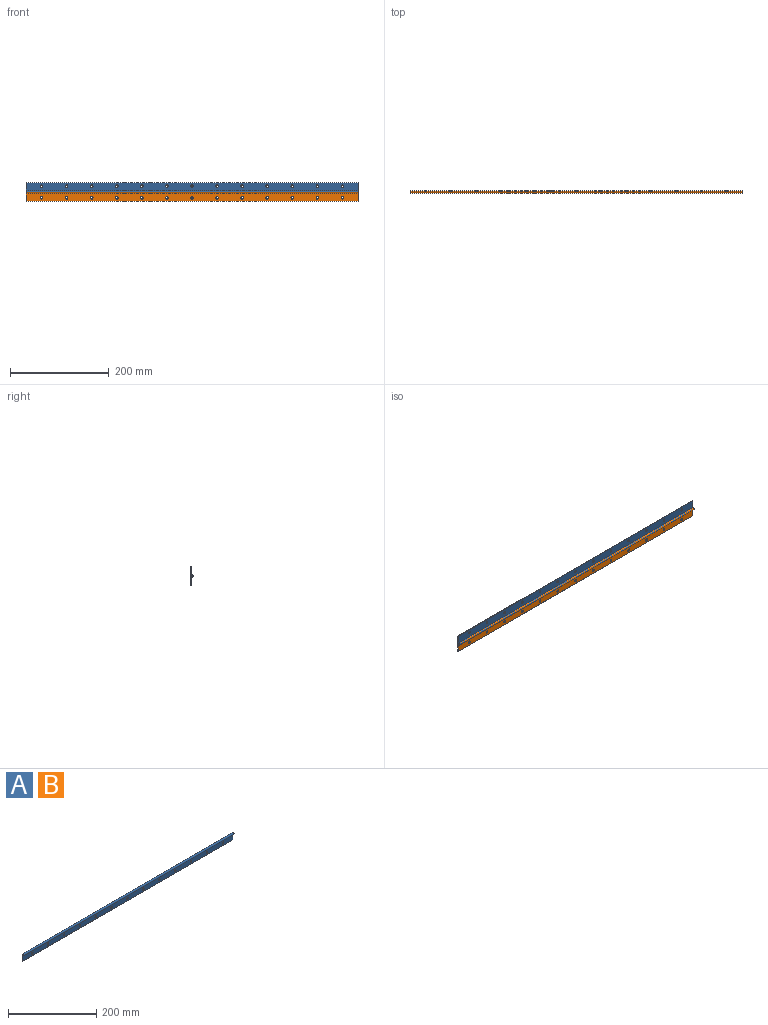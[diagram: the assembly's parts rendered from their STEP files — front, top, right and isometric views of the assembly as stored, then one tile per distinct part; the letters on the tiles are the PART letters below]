
ASSEMBLY  parts=2 mates=1
PART A: 20 faces, bbox 673.1x4.8x21.1 mm
  f0: cylinder r=2.39mm len=673.1mm, axis (-1,0,0), area 8556.7mm2, adj f1,f4,f5,f6
  f1: plane 673.1x16.8mm, normal (0,-1,0), area 11047mm2, adj f0,f2,f5,f6,f7,f8,f9,f10
  f2: plane 673.1x1.02mm, normal (0,0,-1), area 683.9mm2, adj f1,f4,f5,f6
  f3: cylinder r=0.44mm len=673.1mm, axis (-1,0,0), area 1879.9mm2, adj f5,f6
  f4: plane 673.1x18.76mm, normal (0,1,0), area 12362.5mm2, adj f0,f2,f5,f6,f7,f8,f9,f10
  f5: plane 21.15x4.78mm, normal (1,0,0), area 35mm2, adj f0,f1,f2,f3,f4
  f6: plane 21.15x4.78mm, normal (-1,0,0), area 35mm2, adj f0,f1,f2,f3,f4
  f7: cylinder r=2.54mm len=5.08mm, axis (0,-1,0), area 16.2mm2, adj f1,f4
  f8: cylinder r=2.54mm len=5.08mm, axis (0,-1,0), area 16.2mm2, adj f1,f4
  f9: cylinder r=2.54mm len=5.08mm, axis (0,-1,0), area 16.2mm2, adj f1,f4
  f10: cylinder r=2.54mm len=5.08mm, axis (0,-1,0), area 16.2mm2, adj f1,f4
  f11: cylinder r=2.54mm len=5.08mm, axis (0,-1,0), area 16.2mm2, adj f1,f4
  f12: cylinder r=2.54mm len=5.08mm, axis (0,-1,0), area 16.2mm2, adj f1,f4
  f13: cylinder r=2.54mm len=5.08mm, axis (0,-1,0), area 16.2mm2, adj f1,f4
  f14: cylinder r=2.54mm len=5.08mm, axis (0,-1,0), area 16.2mm2, adj f1,f4
  f15: cylinder r=2.54mm len=5.08mm, axis (0,-1,0), area 16.2mm2, adj f1,f4
  f16: cylinder r=2.54mm len=5.08mm, axis (0,-1,0), area 16.2mm2, adj f1,f4
  f17: cylinder r=2.54mm len=5.08mm, axis (0,-1,0), area 16.2mm2, adj f1,f4
  f18: cylinder r=2.54mm len=5.08mm, axis (0,-1,0), area 16.2mm2, adj f1,f4
  f19: cylinder r=2.54mm len=5.08mm, axis (0,-1,0), area 16.2mm2, adj f1,f4
PART B: same geometry as A
PLACE A rot(axis=(0,-1,0),180deg) t=(0,0,0)mm
PLACE B at identity fixed
MATE revolute B.f0 <-> A.f0  axis (-1,0,0) through (0,-2.39,0)mm
